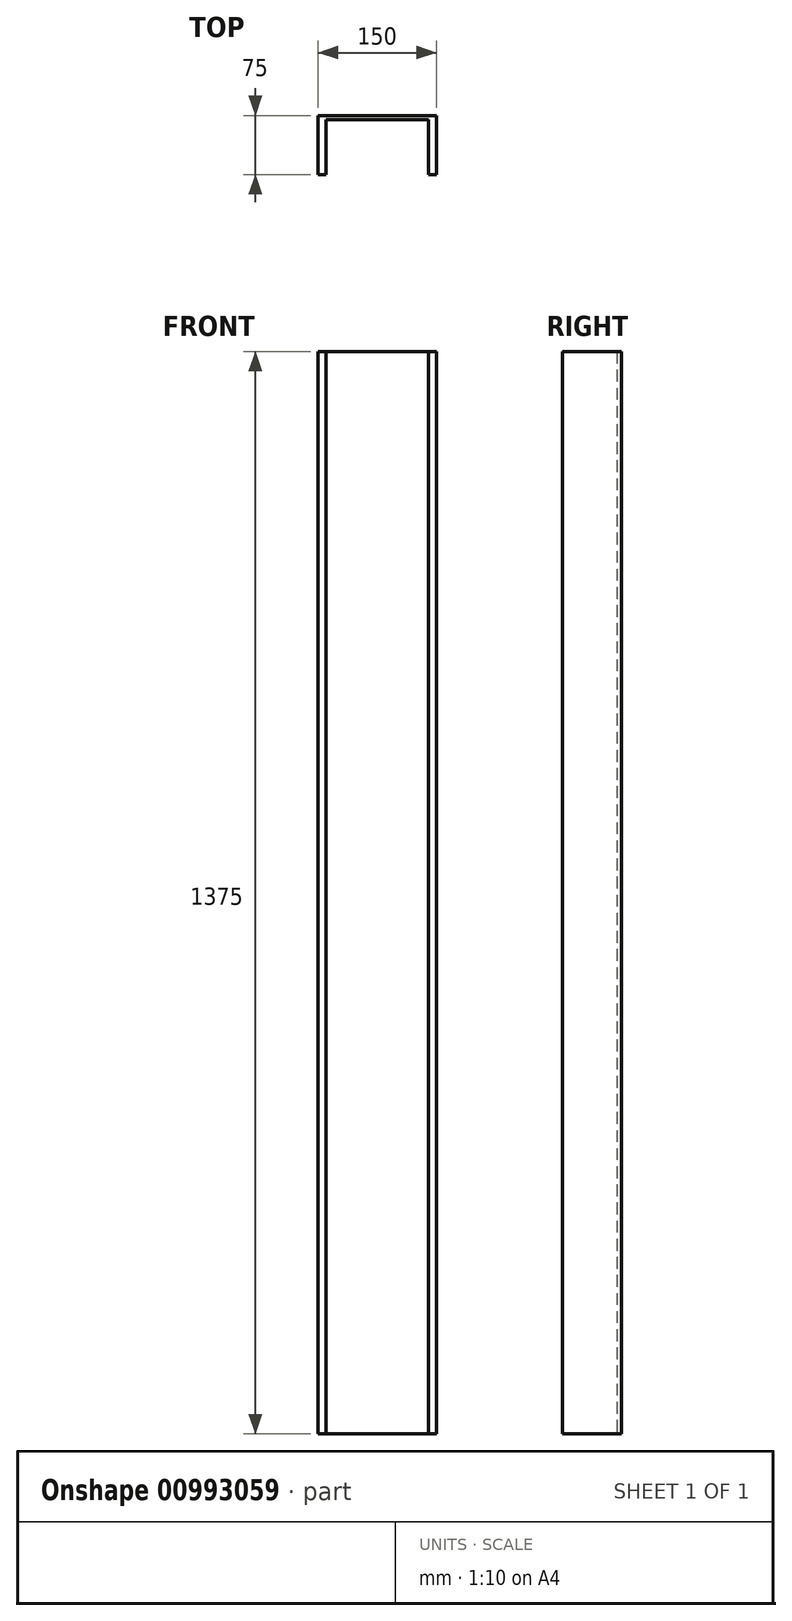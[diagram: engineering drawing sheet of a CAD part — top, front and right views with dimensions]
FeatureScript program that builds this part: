
annotation { "Feature Type Name" : "Feature", "Feature Type Description" : "" }
export const myFeature = defineFeature(function(context is Context, id is Id, definition is map)
    precondition{}
    {
        {
            var Q0;
            Q0=qCreatedBy(makeId("Top.planeOp"),FACE);
            var sketch = newSketch(context, id + "F0", { "sketchPlane" : qUnion([Q0])});
            skLineSegment(sketch, "E0", {"start": v(0, 0) * mm, "end": v(0, 75) * mm});
            skLineSegment(sketch, "E1", {"start": v(0, 75) * mm, "end": v(150, 75) * mm});
            skLineSegment(sketch, "E2", {"start": v(150, 75) * mm, "end": v(150, 0) * mm});
            skLineSegment(sketch, "E3", {"start": v(150, 0) * mm, "end": v(140, 0) * mm});
            skLineSegment(sketch, "E4", {"start": v(140, 0) * mm, "end": v(140, 69.5) * mm});
            skLineSegment(sketch, "E5", {"start": v(140, 69.5) * mm, "end": v(10, 69.5) * mm});
            skLineSegment(sketch, "E6", {"start": v(10, 69.5) * mm, "end": v(10, 0) * mm});
            skLineSegment(sketch, "E7", {"start": v(10, 0) * mm, "end": v(0, 0) * mm});
            skSolve(sketch);
        }
        {
            var Q0;
            Q0=makeQuery(id+"F0.imprint","IMPRINT",FACE,{"disambiguationData":[TD([[makeQuery(id+"F0.imprint","IMPRINT",EDGE,{"derivedFrom":sQuery(id+"F0.wireOp",EDGE,"E0")}),-1.0]])]});
            extrude(context, id + "F1", {"entities" : qUnion([Q0]), "depth" : 1375 * mm, "offsetDistance" : 25 * mm});
        }
    });
